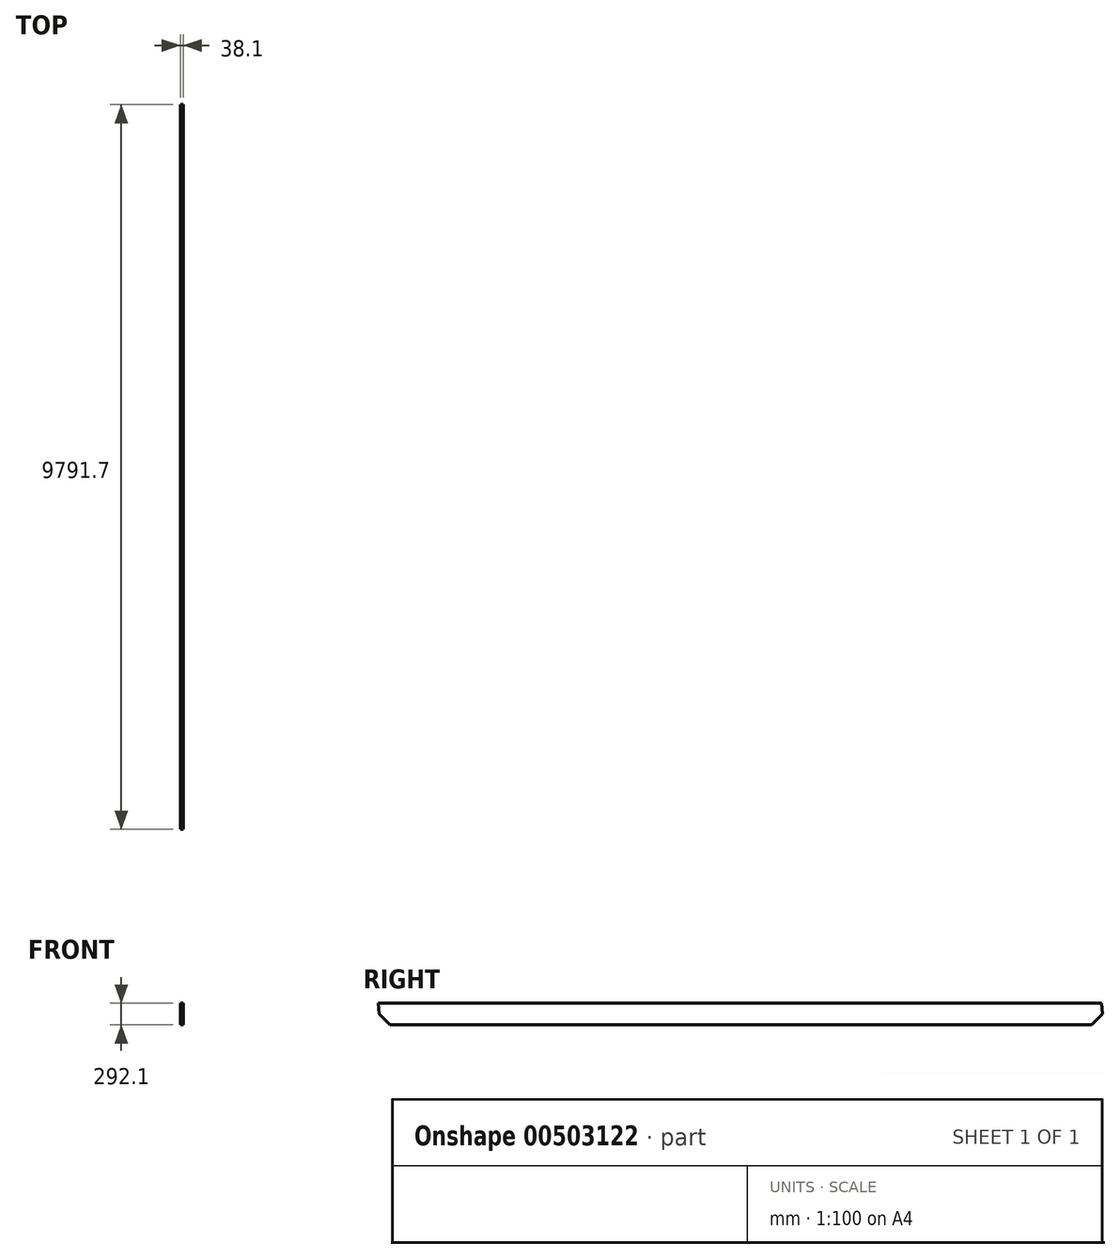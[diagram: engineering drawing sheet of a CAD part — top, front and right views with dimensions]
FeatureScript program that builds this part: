
annotation { "Feature Type Name" : "Feature", "Feature Type Description" : "" }
export const myFeature = defineFeature(function(context is Context, id is Id, definition is map)
    precondition{}
    {
        {
            var Q0;
            Q0=qCreatedBy(makeId("Front.planeOp"),FACE);
            var sketch = newSketch(context, id + "F0", { "sketchPlane" : qUnion([Q0])});
            skLineSegment(sketch, "E0.bottom", {"start": v(0, 0) * mm, "end": v(-38.1, 0) * mm});
            skLineSegment(sketch, "E0.top", {"start": v(0, 292.1) * mm, "end": v(-38.1, 292.1) * mm});
            skLineSegment(sketch, "E0.left", {"start": v(0, 0) * mm, "end": v(0, 292.1) * mm});
            skLineSegment(sketch, "E0.right", {"start": v(-38.1, 0) * mm, "end": v(-38.1, 292.1) * mm});
            skSolve(sketch);
        }
        {
            var Q0;
            Q0 = qSketchRegion(id + "F0", true);
            extrude(context, id + "F1", {"entities" : qUnion([Q0]), "depth" : 9791.7 * mm});
        }
        {
            var Q0;
            Q0=makeQuery(id+"F1.opExtrude","SWEPT_FACE",FACE,{"disambiguationData":[OSD([sQuery(id+"F0.wireOp",EDGE,"E0.left")])]});
            var sketch = newSketch(context, id + "F2", { "sketchPlane" : qUnion([Q0])});
            skLineSegment(sketch, "E1", {"start": v(-9791.7, 292.1) * mm, "end": v(-9779.23, 146.05) * mm});
            skLineSegment(sketch, "E2", {"start": v(-9779.23, 146.05) * mm, "end": v(-9633.18, 0) * mm});
            skLineSegment(sketch, "E3", {"start": v(-9633.18, 0) * mm, "end": v(-9791.7, 0) * mm});
            skLineSegment(sketch, "E4", {"start": v(-9791.7, 0) * mm, "end": v(-9791.7, 292.1) * mm});
            skSolve(sketch);
        }
        {
            var Q0;
            Q0 = qSketchRegion(id + "F2", true);
            extrude(context, id + "F3", {"entities" : qUnion([Q0]), "operationType" : NewBodyOperationType.REMOVE, "endBound" : BoundingType.THROUGH_ALL, "oppositeDirection" : true, "depth" : 25.4 * mm});
        }
        {
            var Q0;
            Q0=makeQuery(id+"F1.opExtrude","SWEPT_FACE",FACE,{"disambiguationData":[OSD([sQuery(id+"F0.wireOp",EDGE,"E0.left")])]});
            var sketch = newSketch(context, id + "F4", { "sketchPlane" : qUnion([Q0])});
            skLineSegment(sketch, "E5", {"start": v(0, 0) * mm, "end": v(0, 146.05) * mm});
            skLineSegment(sketch, "E6", {"start": v(0, 146.05) * mm, "end": v(-146.05, 0) * mm});
            skLineSegment(sketch, "E7", {"start": v(-146.05, 0) * mm, "end": v(0, 0) * mm});
            skLineSegment(sketch, "E8", {"start": v(0, 146.05) * mm, "end": v(0, 292.1) * mm});
            skLineSegment(sketch, "E9", {"start": v(0, 292.1) * mm, "end": v(-12.47, 292.1) * mm});
            skLineSegment(sketch, "E10", {"start": v(-12.47, 292.1) * mm, "end": v(0, 146.05) * mm});
            skSolve(sketch);
        }
        {
            var Q0;
            Q0 = qSketchRegion(id + "F4", true);
            extrude(context, id + "F5", {"entities" : qUnion([Q0]), "operationType" : NewBodyOperationType.REMOVE, "endBound" : BoundingType.THROUGH_ALL, "oppositeDirection" : true, "depth" : 25.4 * mm});
        }
    });
